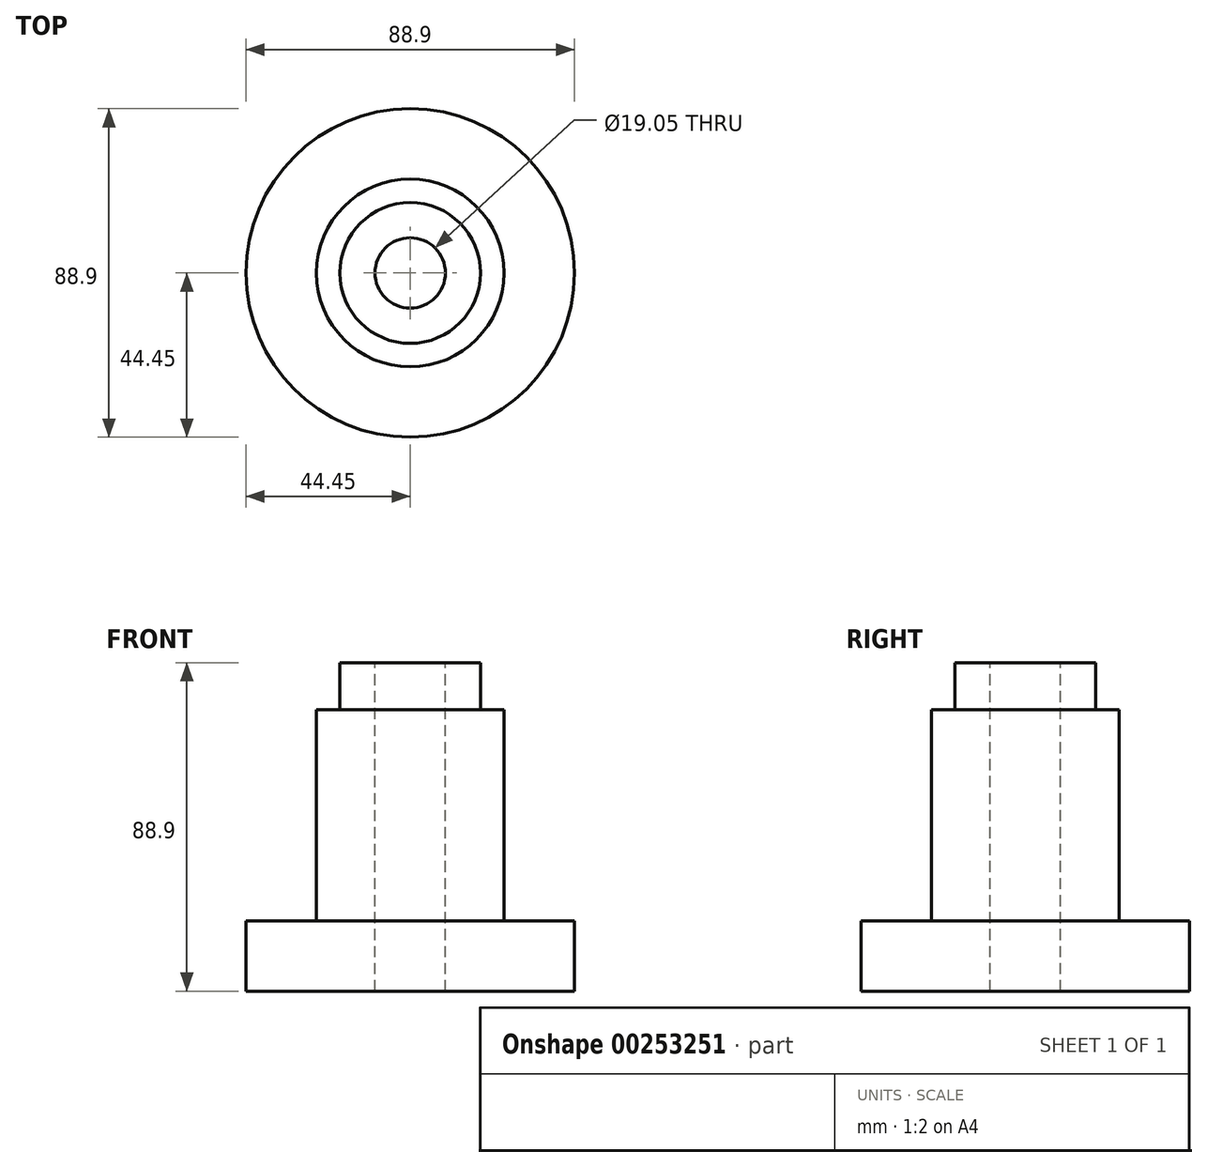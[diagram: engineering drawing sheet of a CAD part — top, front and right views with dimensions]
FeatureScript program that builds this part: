
annotation { "Feature Type Name" : "Feature", "Feature Type Description" : "" }
export const myFeature = defineFeature(function(context is Context, id is Id, definition is map)
    precondition{}
    {
        {
            var Q0;
            Q0=qCreatedBy(makeId("Right.planeOp"),FACE);
            var sketch = newSketch(context, id + "F0", { "sketchPlane" : qUnion([Q0])});
            skLineSegment(sketch, "E0", {"start": v(0, 0) * mm, "end": v(44.45, 0) * mm});
            skLineSegment(sketch, "E1", {"start": v(0, 0) * mm, "end": v(0, 19.05) * mm});
            skLineSegment(sketch, "E2", {"start": v(44.45, 0) * mm, "end": v(44.45, 19.05) * mm});
            skLineSegment(sketch, "E3", {"start": v(0, 19.05) * mm, "end": v(25.4, 19.05) * mm, "construction": true});
            skLineSegment(sketch, "E4", {"start": v(0, 19.05) * mm, "end": v(0, 76.2) * mm});
            skLineSegment(sketch, "E5", {"start": v(25.4, 19.05) * mm, "end": v(25.4, 76.2) * mm});
            skLineSegment(sketch, "E6", {"start": v(25.4, 19.05) * mm, "end": v(44.45, 19.05) * mm});
            skLineSegment(sketch, "E7", {"start": v(0, 76.2) * mm, "end": v(0, 88.9) * mm});
            skLineSegment(sketch, "E8", {"start": v(19.05, 76.2) * mm, "end": v(19.05, 88.9) * mm});
            skLineSegment(sketch, "E9", {"start": v(19.05, 88.9) * mm, "end": v(0, 88.9) * mm});
            skLineSegment(sketch, "E10", {"start": v(19.05, 76.2) * mm, "end": v(25.4, 76.2) * mm});
            skLineSegment(sketch, "E11", {"start": v(19.05, 76.2) * mm, "end": v(0, 76.2) * mm, "construction": true});
            skSolve(sketch);
        }
        {
            var Q0;
            Q0=makeQuery(id+"F0.imprint","IMPRINT",FACE,{"disambiguationData":[TD([[makeQuery(id+"F0.imprint","IMPRINT",EDGE,{"derivedFrom":sQuery(id+"F0.wireOp",EDGE,"E0")}),1.0]])]});
            var Q1;
            Q1=sQuery(id+"F0.wireOp",EDGE,"E1");
            revolve(context, id + "F1", {"entities" : qUnion([Q0]), "axis" : qUnion([Q1]), "revolveType" : RevolveType.FULL});
        }
        {
            var Q0;
            Q0=makeQuery(id+"F1.opRevolve","SWEPT_FACE",FACE,{"disambiguationData":[OSD([sQuery(id+"F0.wireOp",EDGE,"E9")])]});
            var sketch = newSketch(context, id + "F2", { "sketchPlane" : qUnion([Q0])});
            skCircle(sketch, "E12", {"center": v(0, 0) * mm, "radius": 19.05 * mm});
            skCircle(sketch, "E13", {"center": v(0, 0) * mm, "radius": 9.53 * mm});
            skSolve(sketch);
        }
        {
            var Q0;
            Q0=makeQuery(id+"F2.imprint","IMPRINT",FACE,{"disambiguationData":[TD([[makeQuery(id+"F2.imprint","IMPRINT",EDGE,{"derivedFrom":sQuery(id+"F2.wireOp",EDGE,"E13")}),1.0]])]});
            extrude(context, id + "F3", {"entities" : qUnion([Q0]), "operationType" : NewBodyOperationType.REMOVE, "endBound" : BoundingType.THROUGH_ALL, "oppositeDirection" : true, "depth" : 25.4 * mm});
        }
    });
